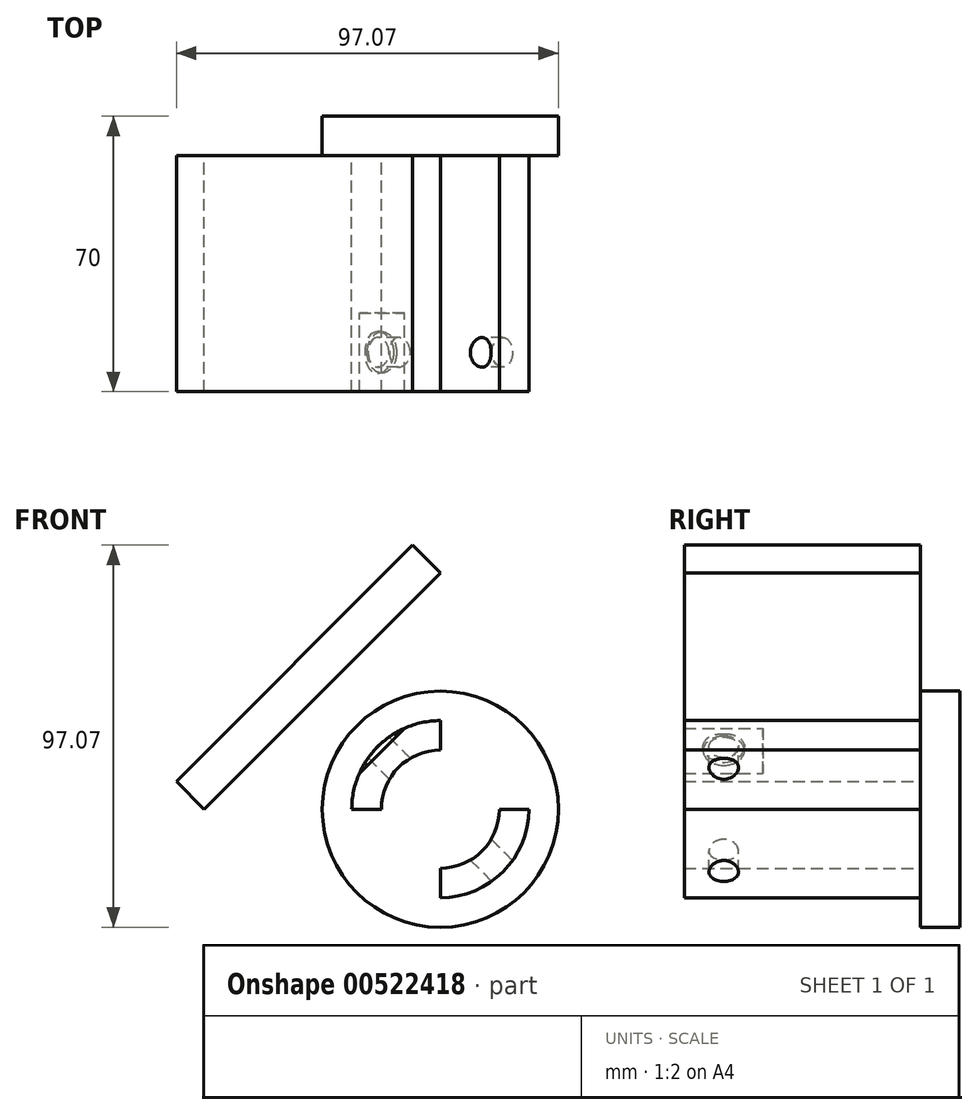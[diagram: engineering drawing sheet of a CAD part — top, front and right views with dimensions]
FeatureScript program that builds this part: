
annotation { "Feature Type Name" : "Feature", "Feature Type Description" : "" }
export const myFeature = defineFeature(function(context is Context, id is Id, definition is map)
    precondition{}
    {
        {
            var Q0;
            Q0=qCreatedBy(makeId("Front.planeOp"),FACE);
            var sketch = newSketch(context, id + "F0", { "sketchPlane" : qUnion([Q0])});
            skCircle(sketch, "E0", {"center": v(0, 0) * mm, "radius": 30 * mm});
            skArc(sketch, "E1", {"start": v(0, 15) * mm, "mid": v(-10.6, 10.6) * mm, "end": v(-15, 0) * mm});
            skArc(sketch, "E2", {"start": v(0, 22.5) * mm, "mid": v(-15.9, 15.9) * mm, "end": v(-22.5, 0) * mm});
            skLineSegment(sketch, "E3", {"start": v(0, 15) * mm, "end": v(0, 22.5) * mm});
            skLineSegment(sketch, "E4", {"start": v(0, 22.5) * mm, "end": v(0, 30) * mm, "construction": true});
            skLineSegment(sketch, "E5", {"start": v(-22.5, 0) * mm, "end": v(-15, 0) * mm});
            skLineSegment(sketch, "E6", {"start": v(0, -15) * mm, "end": v(0, -22.5) * mm});
            skLineSegment(sketch, "E7", {"start": v(15, 0) * mm, "end": v(22.5, 0) * mm});
            skArc(sketch, "E8.trimOffspring", {"start": v(0, -15) * mm, "mid": v(10.6, -10.6) * mm, "end": v(15, 0) * mm});
            skArc(sketch, "E9.trimOffspring", {"start": v(0, -22.5) * mm, "mid": v(15.9, -15.9) * mm, "end": v(22.5, 0) * mm});
            skCircle(sketch, "E10", {"center": v(0, 0) * mm, "radius": 22.5 * mm, "construction": true});
            skSolve(sketch);
        }
        {
            var Q0;
            Q0=makeQuery(id+"F0.imprint","IMPRINT",FACE,{"disambiguationData":[TD([[makeQuery(id+"F0.imprint","IMPRINT",EDGE,{"derivedFrom":sQuery(id+"F0.wireOp",EDGE,"E1")}),-1.0]])]});
            var Q1;
            Q1=makeQuery(id+"F0.imprint","IMPRINT",FACE,{"disambiguationData":[TD([[makeQuery(id+"F0.imprint","IMPRINT",EDGE,{"derivedFrom":sQuery(id+"F0.wireOp",EDGE,"E6")}),1.0]])]});
            extrude(context, id + "F1", {"entities" : qUnion([Q0, Q1]), "depth" : 60 * mm, "offsetDistance" : 25 * mm});
        }
        {
            var Q0;
            Q0=makeQuery(id+"F0.imprint","IMPRINT",FACE,{"disambiguationData":[TD([[makeQuery(id+"F0.imprint","IMPRINT",EDGE,{"derivedFrom":sQuery(id+"F0.wireOp",EDGE,"E0")}),1.0]])]});
            var Q1;
            Q1=makeQuery(id+"F0.imprint","IMPRINT",FACE,{"disambiguationData":[TD([[makeQuery(id+"F0.imprint","IMPRINT",EDGE,{"derivedFrom":sQuery(id+"F0.wireOp",EDGE,"E1")}),-1.0]])]});
            var Q2;
            Q2=makeQuery(id+"F0.imprint","IMPRINT",FACE,{"disambiguationData":[TD([[makeQuery(id+"F0.imprint","IMPRINT",EDGE,{"derivedFrom":sQuery(id+"F0.wireOp",EDGE,"E6")}),1.0]])]});
            extrude(context, id + "F2", {"entities" : qUnion([Q0, Q1, Q2]), "oppositeDirection" : true, "depth" : 10 * mm, "offsetDistance" : 25 * mm});
        }
        {
            var Q0;
            Q0=qCreatedBy(makeId("Front.planeOp"),FACE);
            var sketch = newSketch(context, id + "F3", { "sketchPlane" : qUnion([Q0])});
            skLineSegment(sketch, "E11", {"start": v(0, 0) * mm, "end": v(0, 60) * mm, "construction": true});
            skLineSegment(sketch, "E12", {"start": v(0, 0) * mm, "end": v(-60, 0) * mm, "construction": true});
            skLineSegment(sketch, "E13", {"start": v(0, 60) * mm, "end": v(-60, 0) * mm});
            skLineSegment(sketch, "E14", {"start": v(-67.07, 7.07) * mm, "end": v(-60, 0) * mm});
            skLineSegment(sketch, "E15", {"start": v(-67.07, 7.07) * mm, "end": v(-7.07, 67.07) * mm});
            skLineSegment(sketch, "E16", {"start": v(-7.07, 67.07) * mm, "end": v(0, 60) * mm});
            skCircle(sketch, "E17", {"center": v(0, 0) * mm, "radius": 30 * mm, "construction": true});
            skLineSegment(sketch, "E18", {"start": v(-30, 30) * mm, "end": v(-15.9, 15.9) * mm});
            skCircle(sketch, "E19", {"center": v(0, 0) * mm, "radius": 22.5 * mm, "construction": true});
            skLineSegment(sketch, "E20", {"start": v(-15.9, 15.9) * mm, "end": v(0, 0) * mm});
            skSolve(sketch);
        }
        {
            var Q0;
            Q0 = qSketchRegion(id + "F3", true);
            extrude(context, id + "F4", {"entities" : qUnion([Q0]), "depth" : 60 * mm, "offsetDistance" : 25 * mm});
        }
        {
            var Q0;
            Q0=makeQuery(id+"F4.opExtrude","SWEPT_FACE",FACE,{"disambiguationData":[OSD([sQuery(id+"F3.wireOp",EDGE,"E13")])]});
            var sketch = newSketch(context, id + "F5", { "sketchPlane" : qUnion([Q0])});
            skLineSegment(sketch, "E21.bottom", {"start": v(-60, -42.43) * mm, "end": v(-40, -42.43) * mm});
            skLineSegment(sketch, "E21.top", {"start": v(-60, 42.43) * mm, "end": v(-40, 42.43) * mm});
            skLineSegment(sketch, "E21.left", {"start": v(-60, -42.43) * mm, "end": v(-60, 42.43) * mm});
            skLineSegment(sketch, "E21.right", {"start": v(-40, -42.43) * mm, "end": v(-40, 42.43) * mm});
            skLineSegment(sketch, "E22", {"start": v(-60, 0) * mm, "end": v(-40, 0) * mm});
            skCircle(sketch, "E23", {"center": v(-50, 0) * mm, "radius": 3.75 * mm});
            skCircle(sketch, "E24", {"center": v(-50, 0) * mm, "radius": 5.25 * mm});
            skSolve(sketch);
        }
        {
            var Q0;
            {var subQ0=sQuery(id+"F5.wireOp",EDGE,"E23");var subQ1=sQuery(id+"F5.wireOp",EDGE,"E22");var subQ2=makeQuery(id+"F5.imprint","INTERSECT",VERTEX,{"disambiguationData":[OD(0.0)],"derivedFrom":[subQ1,subQ0]});Q0=makeQuery(id+"F5.imprint","IMPRINT",FACE,{"disambiguationData":[TD([[makeQuery(id+"F5.imprint","IMPRINT",EDGE,{"disambiguationData":[TD([[subQ2,-1.0]])],"derivedFrom":subQ1}),-1.0]])]});}
            var Q1;
            {var subQ0=sQuery(id+"F5.wireOp",EDGE,"E23");var subQ1=sQuery(id+"F5.wireOp",EDGE,"E22");var subQ2=makeQuery(id+"F5.imprint","INTERSECT",VERTEX,{"disambiguationData":[OD(0.0)],"derivedFrom":[subQ1,subQ0]});Q1=makeQuery(id+"F5.imprint","IMPRINT",FACE,{"disambiguationData":[TD([[makeQuery(id+"F5.imprint","IMPRINT",EDGE,{"disambiguationData":[TD([[subQ2,-1.0]])],"derivedFrom":subQ1}),1.0]])]});}
            extrude(context, id + "F6", {"entities" : qUnion([Q0, Q1]), "operationType" : NewBodyOperationType.REMOVE, "depth" : 75 * mm, "offsetDistance" : 25 * mm});
        }
        {
            var Q0;
            {var subQ0=sQuery(id+"F5.wireOp",EDGE,"E24");var subQ1=sQuery(id+"F5.wireOp",EDGE,"E22");var subQ2=makeQuery(id+"F5.imprint","INTERSECT",VERTEX,{"disambiguationData":[OD(0.0)],"derivedFrom":[subQ1,subQ0]});Q0=makeQuery(id+"F5.imprint","IMPRINT",FACE,{"disambiguationData":[TD([[makeQuery(id+"F5.imprint","IMPRINT",EDGE,{"disambiguationData":[TD([[subQ2,-1.0]])],"derivedFrom":subQ1}),1.0]])]});}
            var Q1;
            {var subQ0=sQuery(id+"F5.wireOp",EDGE,"E24");var subQ1=sQuery(id+"F5.wireOp",EDGE,"E22");var subQ2=makeQuery(id+"F5.imprint","INTERSECT",VERTEX,{"disambiguationData":[OD(0.0)],"derivedFrom":[subQ1,subQ0]});Q1=makeQuery(id+"F5.imprint","IMPRINT",FACE,{"disambiguationData":[TD([[makeQuery(id+"F5.imprint","IMPRINT",EDGE,{"disambiguationData":[TD([[subQ2,-1.0]])],"derivedFrom":subQ1}),-1.0]])]});}
            extrude(context, id + "F7", {"entities" : qUnion([Q0, Q1]), "operationType" : NewBodyOperationType.REMOVE, "depth" : 19.93 * mm + 1.5 * mm, "offsetDistance" : 25 * mm});
        }
    });
